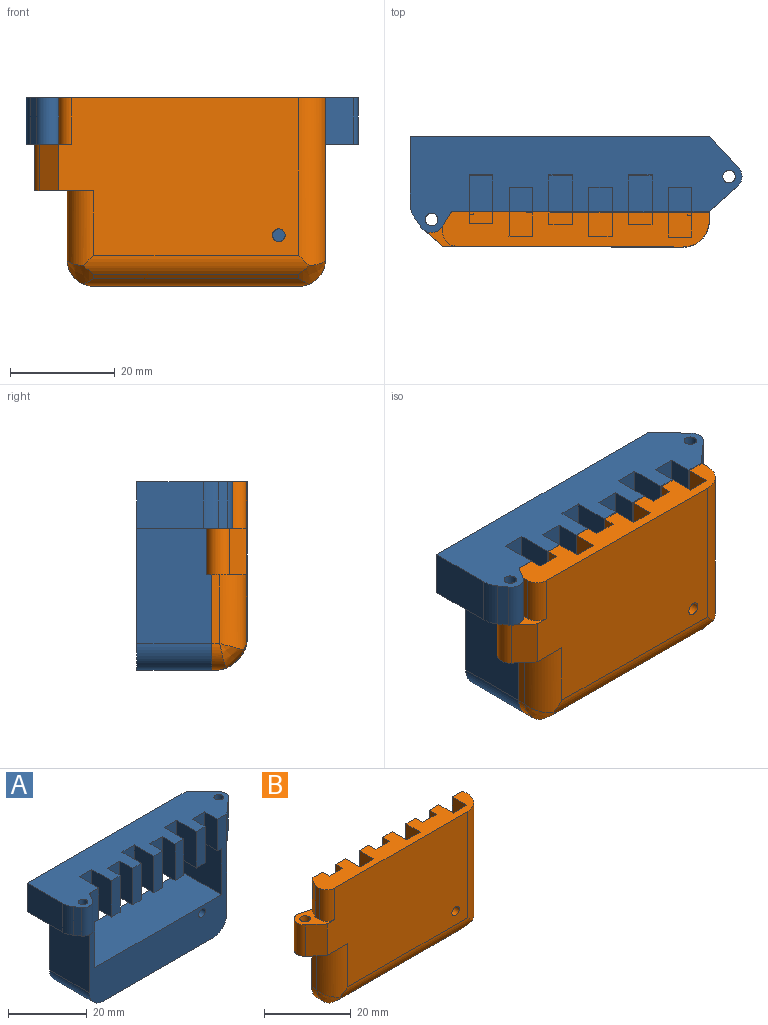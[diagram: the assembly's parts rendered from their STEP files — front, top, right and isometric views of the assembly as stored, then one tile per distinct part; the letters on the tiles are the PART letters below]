
ASSEMBLY  parts=2 mates=1
PART A: 62 faces, bbox 63.4x18.3x36 mm
  f0: plane 49.31x35.98mm, normal (0,-1,0), area 690.8mm2, adj f1,f3,f11,f13,f14,f17,f18,f31
  f1: plane 45.4x14.29mm, normal (0,0,1), area 648.7mm2, adj f0,f2,f17,f51
  f2: plane 57.19x35.98mm, normal (0,1,0), area 1247.9mm2, adj f1,f5,f11,f12,f13,f14,f17,f18
  f3: plane 9.8x4.6mm, normal (-1,0,0), area 45mm2, adj f0,f4,f13,f50
  f4: plane 11.32x4.45mm, normal (0,-1,0), area 49mm2, adj f3,f5,f13,f42,f49,f50
  f5: plane 40.83x14.29mm, normal (0,0,-1), area 438.7mm2, adj f2,f4,f6,f7,f8,f9,f10,f12
  f6: plane 11.32x3.18mm, normal (0,-1,0), area 35.9mm2, adj f5,f13,f28,f29,f39,f48
  f7: plane 11.32x3.18mm, normal (0,-1,0), area 35.9mm2, adj f5,f13,f22,f23,f41,f45
  f8: plane 11.32x3.18mm, normal (0,-1,0), area 35.9mm2, adj f5,f13,f25,f26,f46,f47
  f9: plane 11.32x3.18mm, normal (0,-1,0), area 35.9mm2, adj f5,f13,f19,f20,f42,f43
  f10: plane 11.32x3.17mm, normal (0,-1,0), area 35.9mm2, adj f5,f13,f15,f44
  f11: plane 14.29x2.29mm, normal (0,0,-1), area 27mm2, adj f0,f2,f12,f17,f30,f40
  f12: plane 7.3x1.52mm, normal (-1,0,0), area 11.1mm2, adj f2,f5,f11,f30
  f13: plane 63.41x18.3mm, normal (0,0,1), area 724.3mm2, adj f0,f2,f3,f4,f6,f7,f8,f9
  f14: plane 22.01x14.29mm, normal (-1,0,0), area 314.5mm2, adj f0,f2,f31,f59
  f15: plane 11.32x4.6mm, normal (-1,0,0), area 52.1mm2, adj f5,f10,f13,f16
  f16: plane 11.32x4.45mm, normal (0,-1,0), area 50.4mm2, adj f5,f13,f15,f41
  f17: plane 14.29x14.26mm, normal (1,0,0), area 203.8mm2, adj f0,f1,f2,f11
  f18: plane 39.15x14.29mm, normal (0,0,-1), area 559.4mm2, adj f0,f2,f58,f59
  f19: plane 6.99x0.01mm, normal (0,0,1), area 0mm2, adj f9,f20,f21,f43
  f20: plane 11.32x6.99mm, normal (-1,0,0), area 79mm2, adj f9,f13,f19,f21
  f21: plane 11.32x4.45mm, normal (0,-1,0), area 50.4mm2, adj f5,f13,f19,f20,f43,f44
  f22: plane 6.99x0.01mm, normal (0,0,1), area 0mm2, adj f7,f23,f24,f45
  f23: plane 11.32x6.99mm, normal (-1,0,0), area 79mm2, adj f7,f13,f22,f24
  f24: plane 11.32x4.45mm, normal (0,-1,0), area 50.4mm2, adj f5,f13,f22,f23,f45,f46
  f25: plane 4.6x0.01mm, normal (0,0,1), area 0mm2, adj f8,f26,f27,f47
  f26: plane 11.32x4.6mm, normal (-1,0,0), area 52mm2, adj f8,f13,f25,f27
  f27: plane 11.32x4.45mm, normal (0,-1,0), area 50.4mm2, adj f5,f13,f25,f26,f47,f48
  f28: plane 6.99x0.01mm, normal (0,0,1), area 0mm2, adj f6,f29,f30,f39
  f29: plane 11.32x6.99mm, normal (-1,0,0), area 79mm2, adj f6,f13,f28,f30
  f30: plane 11.32x4.45mm, normal (0,-1,0), area 49.2mm2, adj f5,f11,f12,f13,f28,f29,f39,f40
  f31: plane 18.3x8.24mm, normal (0,0,-1), area 128.3mm2, adj f0,f2,f14,f32,f33,f34,f35,f36
  f32: plane 12.68x8.89mm, normal (-1,0,0), area 112.7mm2, adj f2,f13,f31,f36
  f33: plane 8.89x1.64mm, normal (-0.82,-0.58,0), area 17.8mm2, adj f13,f31,f34,f36
  f34: cylinder r=2.48mm len=8.89mm, axis (0,0,1), area 44.2mm2, adj f13,f31,f33,f35
  f35: plane 8.89x2.46mm, normal (0.86,-0.5,0), area 25.3mm2, adj f13,f31,f34,f37
  f36: cylinder r=5.08mm len=8.89mm, axis (0,0,1), area 27.7mm2, adj f13,f31,f32,f33
  f37: cylinder r=0.64mm len=8.89mm, axis (0,0,1), area 5.9mm2, adj f0,f13,f31,f35
  f38: cylinder r=1.21mm len=8.89mm, axis (0,0,1), area 67.4mm2, adj f13,f31
  f39: plane 6.99x0.01mm, normal (-1,0,0), area 0mm2, adj f5,f6,f28,f30
  f40: plane 9.8x6.99mm, normal (1,0,0), area 68.4mm2, adj f0,f11,f13,f30
  f41: plane 11.32x4.6mm, normal (1,0,0), area 52.1mm2, adj f5,f7,f13,f16
  f42: plane 11.32x4.6mm, normal (1,0,0), area 52.1mm2, adj f4,f5,f9,f13
  f43: plane 6.99x0.01mm, normal (-1,0,0), area 0mm2, adj f5,f9,f19,f21
  f44: plane 11.32x6.99mm, normal (1,0,0), area 79.1mm2, adj f5,f10,f13,f21
  f45: plane 6.99x0.01mm, normal (-1,0,0), area 0mm2, adj f5,f7,f22,f24
  f46: plane 11.32x6.99mm, normal (1,0,0), area 79.1mm2, adj f5,f8,f13,f24
  f47: plane 4.6x0.01mm, normal (-1,0,0), area 0mm2, adj f5,f8,f25,f27
  f48: plane 11.32x4.6mm, normal (1,0,0), area 52.1mm2, adj f5,f6,f13,f27
  f49: plane 9.69x1.52mm, normal (1,0,0), area 14.8mm2, adj f2,f4,f5,f50
  f50: plane 14.29x2.29mm, normal (0,0,-1), area 28.5mm2, adj f0,f2,f3,f4,f49,f51
  f51: plane 14.29x14.26mm, normal (-1,0,0), area 203.8mm2, adj f0,f1,f2,f50
  f52: plane 22.01x14.29mm, normal (1,0,0), area 314.5mm2, adj f0,f2,f53,f58
  f53: plane 14.29x6.23mm, normal (0,0,-1), area 46.1mm2, adj f52,f54,f55,f56,f57
  f54: plane 8.89x5.93mm, normal (0.73,0.68,0), area 72.3mm2, adj f2,f13,f53,f55
  f55: cylinder r=2.47mm len=8.89mm, axis (0,0,1), area 35mm2, adj f13,f53,f54,f57
  f56: cylinder r=1.21mm len=8.89mm, axis (0,0,1), area 67.4mm2, adj f13,f53
  f57: plane 8.89x5.4mm, normal (0.67,-0.75,0), area 64.4mm2, adj f0,f13,f53,f55
  f58: cylinder r=5.08mm len=14.29mm, axis (0,-1,0), area 114mm2, adj f0,f2,f18,f52
  f59: cylinder r=5.08mm len=14.29mm, axis (0,1,0), area 114mm2, adj f0,f2,f14,f18
  f60: cylinder r=1.22mm len=8.66mm, axis (0,-1,0), area 66.3mm2, adj f0,f61
  f61: plane 2.44x2.44mm, normal (0,-1,0), area 4.7mm2, adj f60
PART B: 60 faces, bbox 55.6x7.5x36 mm
  f0: plane 49.31x35.99mm, normal (0,1,0), area 1391.1mm2, adj f1,f2,f3,f4,f5,f7,f8,f12
  f1: plane 11.33x2.3mm, normal (1,0,0), area 25.2mm2, adj f0,f2,f7,f14,f55,f59
  f2: plane 4.45x2.3mm, normal (0,0,1), area 9.8mm2, adj f0,f1,f14,f15,f55,f56
  f3: plane 11.33x4.69mm, normal (-1,0,0), area 52.3mm2, adj f0,f4,f7,f16,f50,f52
  f4: plane 4.69x4.45mm, normal (0,0,1), area 20.4mm2, adj f0,f3,f16,f17,f50,f51
  f5: plane 39.15x0.67mm, normal (0,0,-1), area 26.2mm2, adj f0,f41,f42,f47
  f6: plane 45.85x30.08mm, normal (0,-1,0), area 1269.4mm2, adj f7,f11,f36,f37,f38,f40,f43,f48
  f7: plane 50.93x6.58mm, normal (0,0,1), area 232.9mm2, adj f0,f1,f3,f6,f13,f14,f15,f16
  f8: plane 8.89x3.09mm, normal (0.27,0.96,0), area 28.5mm2, adj f0,f9,f11,f36
  f9: cylinder r=2.48mm len=8.89mm, axis (0,0,1), area 60mm2, adj f8,f11,f36,f37
  f10: cylinder r=1.21mm len=8.89mm, axis (0,0,1), area 67.4mm2, adj f11,f36
  f11: plane 11.32x7.54mm, normal (0,0,-1), area 35.9mm2, adj f6,f8,f9,f10,f12,f37,f43
  f12: plane 13.13x1.5mm, normal (-1,0,0), area 19.7mm2, adj f0,f11,f42,f43
  f13: plane 8.89x1.27mm, normal (-1,0,0), area 11.3mm2, adj f7,f34,f36,f38
  f14: plane 11.33x4.45mm, normal (0,1,0), area 50.4mm2, adj f1,f2,f7,f15
  f15: plane 11.33x2.3mm, normal (-1,0,0), area 26mm2, adj f0,f2,f7,f14
  f16: plane 11.33x4.45mm, normal (0,1,0), area 50.4mm2, adj f3,f4,f7,f17
  f17: plane 11.33x4.69mm, normal (1,0,0), area 53.1mm2, adj f0,f4,f7,f16
  f18: plane 11.33x4.45mm, normal (0,1,0), area 50.4mm2, adj f7,f19,f20,f21
  f19: plane 11.33x2.3mm, normal (-1,0,0), area 26mm2, adj f0,f7,f18,f21
  f20: plane 11.33x2.3mm, normal (1,0,0), area 26mm2, adj f0,f7,f18,f21
  f21: plane 4.45x2.3mm, normal (0,0,1), area 10.2mm2, adj f0,f18,f19,f20
  f22: plane 11.33x4.45mm, normal (0,1,0), area 50.4mm2, adj f7,f23,f24,f25
  f23: plane 11.33x4.69mm, normal (-1,0,0), area 53.1mm2, adj f0,f7,f22,f25
  f24: plane 11.33x4.69mm, normal (1,0,0), area 53.1mm2, adj f0,f7,f22,f25
  f25: plane 4.69x4.45mm, normal (0,0,1), area 20.8mm2, adj f0,f22,f23,f24
  f26: plane 11.33x4.45mm, normal (0,1,0), area 50.4mm2, adj f7,f27,f28,f29
  f27: plane 11.33x2.3mm, normal (-1,0,0), area 26mm2, adj f0,f7,f26,f29
  f28: plane 11.33x2.3mm, normal (1,0,0), area 26mm2, adj f0,f7,f26,f29
  f29: plane 4.45x2.3mm, normal (0,0,1), area 10.2mm2, adj f0,f26,f27,f28
  f30: plane 11.33x4.45mm, normal (0,1,0), area 50.4mm2, adj f7,f31,f32,f33
  f31: plane 11.33x4.69mm, normal (-1,0,0), area 53.1mm2, adj f0,f7,f30,f33
  f32: plane 11.33x4.69mm, normal (1,0,0), area 53.1mm2, adj f0,f7,f30,f33
  f33: plane 4.69x4.45mm, normal (0,0,1), area 20.8mm2, adj f0,f30,f31,f32
  f34: plane 8.89x2.46mm, normal (-0.86,0.5,0), area 25.3mm2, adj f7,f13,f35,f36
  f35: cylinder r=0.64mm len=8.89mm, axis (0,0,1), area 5.9mm2, adj f0,f7,f34,f36
  f36: plane 7.54x7.17mm, normal (0,0,1), area 23.4mm2, adj f0,f6,f8,f9,f10,f13,f34,f35
  f37: plane 8.89x3.75mm, normal (-0.64,-0.76,0), area 43.6mm2, adj f6,f9,f11,f36
  f38: cylinder r=2.54mm len=8.89mm, axis (0,0,1), area 35.5mm2, adj f6,f7,f13,f36
  f39: plane 30.91x1.5mm, normal (1,0,0), area 46.4mm2, adj f0,f7,f40,f41
  f40: cylinder r=5.08mm len=32.08mm, axis (0,0,1), area 250.5mm2, adj f6,f7,f39,f44,f48
  f41: cylinder r=5.08mm len=5.08mm, axis (0,-1,0), area 16.2mm2, adj f0,f5,f39,f44,f47
  f42: cylinder r=5.08mm len=5.08mm, axis (0,-1,0), area 16.2mm2, adj f0,f5,f12,f46,f47
  f43: cylinder r=5.08mm len=14.3mm, axis (0,0,-1), area 108.6mm2, adj f6,f11,f12,f46,f48
  f44: bspline ~5.09x5.09mm, area 22.1mm2, adj f40,f41,f45,f47,f48
  f45: plane 39.15x0.83mm, normal (0,-0.71,-0.71), area 46.2mm2, adj f44,f46,f47,f48
  f46: bspline ~5.09x5.09mm, area 22.1mm2, adj f42,f43,f45,f47,f48
  f47: cylinder r=5.08mm len=43.15mm, axis (1,0,0), area 164.2mm2, adj f5,f41,f42,f44,f45,f46
  f48: cylinder r=5.08mm len=43.15mm, axis (-1,0,0), area 164.2mm2, adj f6,f40,f43,f44,f45,f46
  f49: cylinder r=1.22mm len=6.58mm, axis (0,-1,0), area 50.4mm2, adj f0,f6
  f50: plane 14.26x2.29mm, normal (0,1,0), area 31.2mm2, adj f3,f4,f51,f52,f53,f54
  f51: plane 12.73x0.52mm, normal (1,0,0), area 6.6mm2, adj f0,f4,f50,f54
  f52: plane 1.38x0.52mm, normal (0,0,-1), area 0.7mm2, adj f0,f3,f50,f53
  f53: plane 14.26x0.52mm, normal (-1,0,0), area 7.4mm2, adj f0,f50,f52,f54
  f54: plane 2.29x0.52mm, normal (0,0,1), area 1.2mm2, adj f0,f50,f51,f53
  f55: plane 14.26x2.29mm, normal (0,1,0), area 31.4mm2, adj f1,f2,f56,f57,f58,f59
  f56: plane 12.73x0.52mm, normal (-1,0,0), area 6.6mm2, adj f0,f2,f55,f57
  f57: plane 2.29x0.52mm, normal (0,0,1), area 1.2mm2, adj f0,f55,f56,f58
  f58: plane 14.26x0.52mm, normal (1,0,0), area 7.4mm2, adj f0,f55,f57,f59
  f59: plane 1.47x0.52mm, normal (0,0,-1), area 0.8mm2, adj f0,f1,f55,f58
PLACE A t=(73.01,75.54,50.24)mm
PLACE B rot(axis=(0,0,-1),0.2deg) t=(73.01,75.25,50.24)mm
MATE revolute B.f9 <-> A.f34  axis (0,0,1) through (6.54,74.02,58.28)mm
